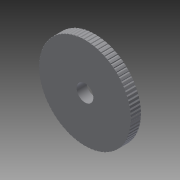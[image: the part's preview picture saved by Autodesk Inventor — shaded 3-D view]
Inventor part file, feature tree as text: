
AUTODESK INVENTOR PART (.ipt)
format: ipt  version: 2014 (Build 180170000, 170)  size: 279,040 bytes
history: native  units: mm
features: extrude x3, sketch x3, pattern_circular x1
ambient origin geometry x8: Origin, YZ Plane, XZ Plane, XY Plane, X Axis, Y Axis, Z Axis, Center Point
bodies: Solid1 (feature_tree)
feature tree (7):
  extrude  "Extrusion1"  Depth=6.0mm TaperAngle=0.0deg
  extrude  "Extrusion2"  Depth=10.0mm TaperAngle=0.0deg
  extrude  "Extrusion3"  Depth=10.0mm TaperAngle=360.0deg
  pattern_circular  "Circular Pattern1"  [2 undecoded]
  sketch  "Sketch1"  dims[d0=55.0mm d1=6.0mm d2=0.0mm]
  sketch  "Sketch2"  dims[d3=10.0mm d4=10.0mm d5=0.0mm]
  sketch  "Sketch3"  dims[d7=10.0mm d8=0.0mm d9=800.0mm d10=360.0deg]
note: 2 required parameter values undecoded (feature->parameter linkage not recoverable at this tier; creation-order binding heuristic only, values carry confidence <= 0.55)
